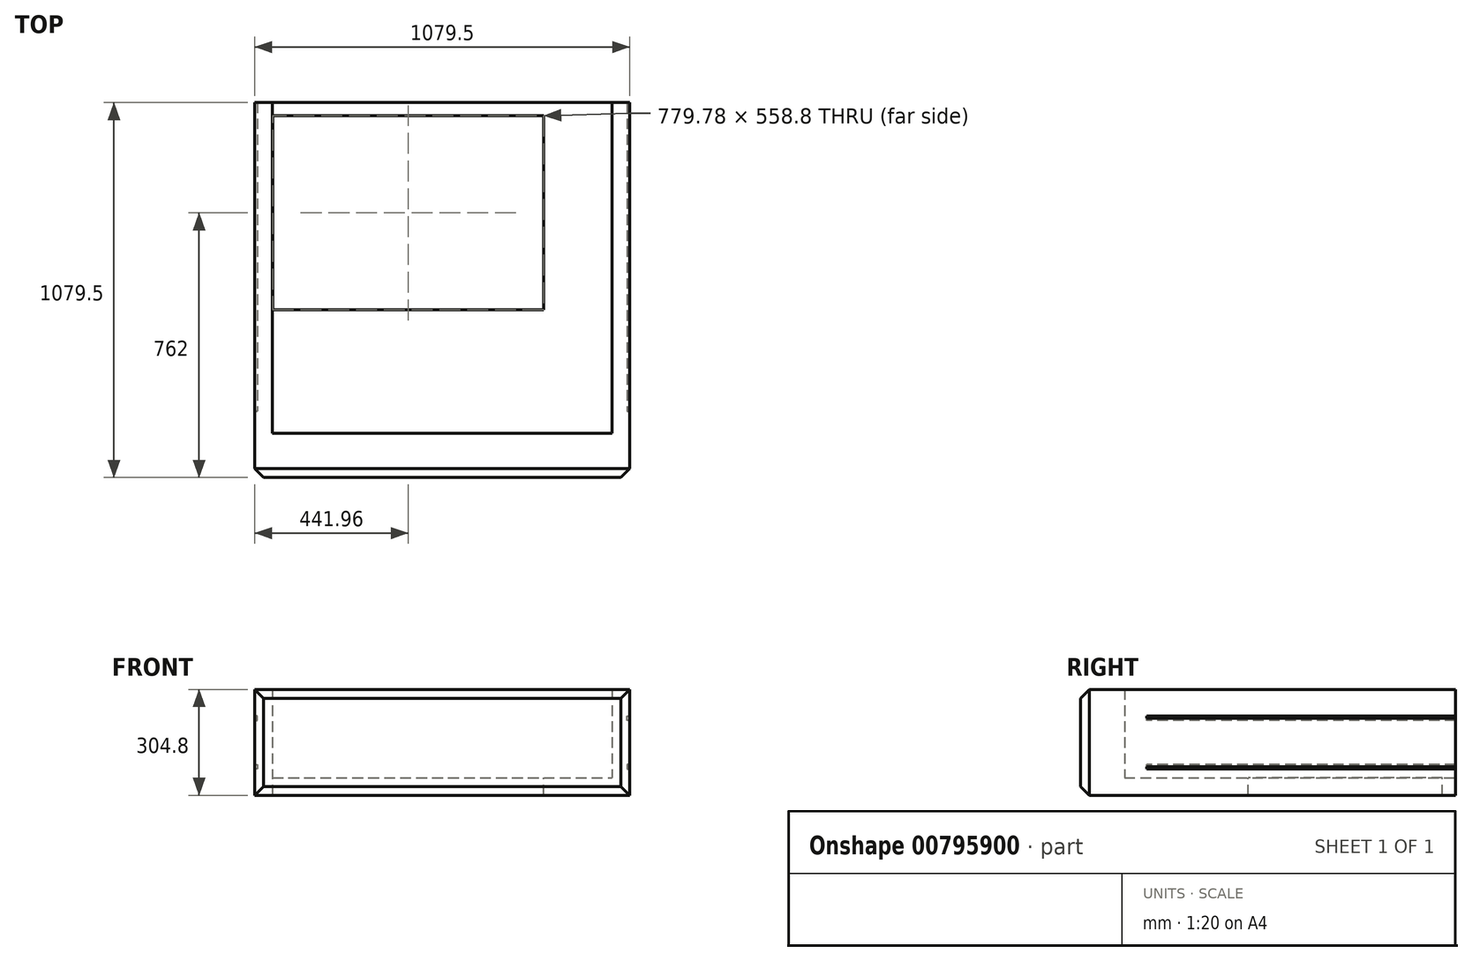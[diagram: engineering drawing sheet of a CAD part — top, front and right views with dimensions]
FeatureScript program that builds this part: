
annotation { "Feature Type Name" : "Feature", "Feature Type Description" : "" }
export const myFeature = defineFeature(function(context is Context, id is Id, definition is map)
    precondition{}
    {
        {
            var Q0;
            Q0=qCreatedBy(makeId("Top.planeOp"),FACE);
            var sketch = newSketch(context, id + "F0", { "sketchPlane" : qUnion([Q0])});
            skLineSegment(sketch, "E0.0", {"start": v(539.75, 254) * mm, "end": v(539.75, -825.5) * mm});
            skLineSegment(sketch, "E0.1", {"start": v(539.75, 254) * mm, "end": v(-539.75, 254) * mm});
            skLineSegment(sketch, "E0.2", {"start": v(-539.75, -825.5) * mm, "end": v(-539.75, 254) * mm});
            skLineSegment(sketch, "E0.3", {"start": v(-539.75, -825.5) * mm, "end": v(539.75, -825.5) * mm});
            skLineSegment(sketch, "E1.bottom", {"start": v(-474.98, 203.2) * mm, "end": v(279.4, 203.2) * mm});
            skLineSegment(sketch, "E1.top", {"start": v(-474.98, -330.2) * mm, "end": v(279.4, -330.2) * mm});
            skLineSegment(sketch, "E1.left", {"start": v(-474.98, 203.2) * mm, "end": v(-474.98, -330.2) * mm});
            skLineSegment(sketch, "E1.right", {"start": v(279.4, 203.2) * mm, "end": v(279.4, -330.2) * mm});
            skSolve(sketch);
        }
        {
            var Q0;
            Q0=makeQuery(id+"F0.imprint","IMPRINT",FACE,{"disambiguationData":[TD([[makeQuery(id+"F0.imprint","IMPRINT",EDGE,{"derivedFrom":sQuery(id+"F0.wireOp",EDGE,"E0.0")}),-1.0]])]});
            var sketch = newSketch(context, id + "F1", { "sketchPlane" : qUnion([Q0])});
            skLineSegment(sketch, "E2.0", {"start": v(539.75, 254) * mm, "end": v(488.95, 254) * mm});
            skLineSegment(sketch, "E2.1", {"start": v(539.75, 254) * mm, "end": v(539.75, -825.5) * mm});
            skLineSegment(sketch, "E2.2", {"start": v(-539.75, -825.5) * mm, "end": v(539.75, -825.5) * mm});
            skLineSegment(sketch, "E2.3", {"start": v(-539.75, -825.5) * mm, "end": v(-539.75, 254) * mm});
            skLineSegment(sketch, "E3.0", {"start": v(-488.95, -698.5) * mm, "end": v(488.95, -698.5) * mm});
            skLineSegment(sketch, "E3.1", {"start": v(-488.95, -698.5) * mm, "end": v(-488.95, 254) * mm});
            skLineSegment(sketch, "E3.3", {"start": v(488.95, 254) * mm, "end": v(488.95, -698.5) * mm});
            skLineSegment(sketch, "E4.trimOffspring", {"start": v(-488.95, 254) * mm, "end": v(-539.75, 254) * mm});
            skSolve(sketch);
        }
        {
            var Q0;
            Q0 = qSketchRegion(id + "F1", true);
            extrude(context, id + "F2", {"entities" : qUnion([Q0]), "depth" : 304.8 * mm, "offsetDistance" : 25.4 * mm});
        }
        {
            var Q0;
            Q0=qCreatedBy(makeId("Top.planeOp"),FACE);
            var sketch = newSketch(context, id + "F3", { "sketchPlane" : qUnion([Q0])});
            skLineSegment(sketch, "E5.bottom", {"start": v(-539.75, 254) * mm, "end": v(539.75, 254) * mm});
            skLineSegment(sketch, "E5.top", {"start": v(-539.75, -825.5) * mm, "end": v(539.75, -825.5) * mm});
            skLineSegment(sketch, "E5.left", {"start": v(-539.75, 254) * mm, "end": v(-539.75, -825.5) * mm});
            skLineSegment(sketch, "E5.right", {"start": v(539.75, 254) * mm, "end": v(539.75, -825.5) * mm});
            skSolve(sketch);
        }
        {
            var Q0;
            Q0 = qSketchRegion(id + "F3", true);
            extrude(context, id + "F4", {"entities" : qUnion([Q0]), "operationType" : NewBodyOperationType.ADD, "depth" : 50.8 * mm, "offsetDistance" : 25.4 * mm});
        }
        {
            var Q0;
            Q0=makeQuery(id+"F2.opExtrude","SWEPT_FACE",FACE,{"disambiguationData":[OSD([sQuery(id+"F1.wireOp",EDGE,"E2.2")])]});
            chamfer(context, id + "F5", {"entities" : qUnion([Q0]), "width" : 25.4 * mm, "tangentPropagation" : true});
        }
        {
            var Q0;
            Q0=makeQuery(id+"F2.opExtrude","SWEPT_FACE",FACE,{"disambiguationData":[OSD([sQuery(id+"F1.wireOp",EDGE,"E2.1")])]});
            var sketch = newSketch(context, id + "F6", { "sketchPlane" : qUnion([Q0])});
            skArc(sketch, "E6", {"start": v(39.93, 203.2) * mm, "mid": v(103.43, 139.7) * mm, "end": v(166.93, 203.2) * mm});
            skLineSegment(sketch, "E7", {"start": v(166.93, 203.2) * mm, "end": v(166.93, 304.8) * mm});
            skLineSegment(sketch, "E8", {"start": v(39.93, 203.2) * mm, "end": v(39.93, 304.8) * mm});
            skSolve(sketch);
        }
        {
            var Q0;
            Q0=makeQuery(id+"F4.opExtrude","CAP_FACE",FACE,{"disambiguationData":[OSD([sQuery(id+"F3.wireOp",EDGE,"E5.bottom"),sQuery(id+"F3.wireOp",EDGE,"E5.top"),sQuery(id+"F3.wireOp",EDGE,"E5.left"),sQuery(id+"F3.wireOp",EDGE,"E5.right")])],"isStart":false});
            var sketch = newSketch(context, id + "F7", { "sketchPlane" : qUnion([Q0])});
            skCircle(sketch, "E9", {"center": v(0, 0) * mm, "radius": 63.5 * mm});
            skSolve(sketch);
        }
        {
            var Q0;
            Q0=makeQuery(id+"F7.imprint","IMPRINT",FACE,{"disambiguationData":[TD([[makeQuery(id+"F7.imprint","IMPRINT",EDGE,{"derivedFrom":sQuery(id+"F7.wireOp",EDGE,"E9")}),1.0]])]});
            extrude(context, id + "F8", {"entities" : qUnion([Q0]), "operationType" : NewBodyOperationType.REMOVE, "endBound" : BoundingType.UP_TO_NEXT, "oppositeDirection" : true, "depth" : 25.4 * mm, "offsetDistance" : 25.4 * mm});
        }
        {
            var Q0;
            Q0=makeQuery(id+"F4.opExtrude","CAP_FACE",FACE,{"disambiguationData":[OSD([sQuery(id+"F3.wireOp",EDGE,"E5.bottom"),sQuery(id+"F3.wireOp",EDGE,"E5.top"),sQuery(id+"F3.wireOp",EDGE,"E5.left"),sQuery(id+"F3.wireOp",EDGE,"E5.right")])],"isStart":false});
            var sketch = newSketch(context, id + "F9", { "sketchPlane" : qUnion([Q0])});
            skLineSegment(sketch, "E10.0", {"start": v(-474.98, 203.2) * mm, "end": v(279.4, 203.2) * mm});
            skLineSegment(sketch, "E10.1", {"start": v(-474.98, 203.2) * mm, "end": v(-474.98, -330.2) * mm});
            skLineSegment(sketch, "E10.2", {"start": v(-474.98, -330.2) * mm, "end": v(279.4, -330.2) * mm});
            skLineSegment(sketch, "E10.3", {"start": v(279.4, 203.2) * mm, "end": v(279.4, -330.2) * mm});
            skLineSegment(sketch, "E11.0", {"start": v(-487.68, 215.9) * mm, "end": v(292.1, 215.9) * mm});
            skLineSegment(sketch, "E11.1", {"start": v(-487.68, 215.9) * mm, "end": v(-487.68, -342.9) * mm});
            skLineSegment(sketch, "E11.2", {"start": v(-487.68, -342.9) * mm, "end": v(292.1, -342.9) * mm});
            skLineSegment(sketch, "E11.3", {"start": v(292.1, 215.9) * mm, "end": v(292.1, -342.9) * mm});
            skSolve(sketch);
        }
        {
            var Q0;
            Q0=makeQuery(id+"F9.imprint","IMPRINT",FACE,{"disambiguationData":[TD([[makeQuery(id+"F9.imprint","IMPRINT",EDGE,{"derivedFrom":sQuery(id+"F9.wireOp",EDGE,"E10.0")}),1.0]])]});
            var Q1;
            Q1=makeQuery(id+"F9.imprint","IMPRINT",FACE,{"disambiguationData":[TD([[makeQuery(id+"F9.imprint","IMPRINT",EDGE,{"derivedFrom":sQuery(id+"F9.wireOp",EDGE,"E10.0")}),-1.0]])]});
            extrude(context, id + "F10", {"entities" : qUnion([Q0, Q1]), "operationType" : NewBodyOperationType.REMOVE, "endBound" : BoundingType.UP_TO_NEXT, "oppositeDirection" : true, "depth" : 25.4 * mm, "offsetDistance" : 25.4 * mm});
        }
        {
            var Q0;
            Q0=qCreatedBy(makeId("Front.planeOp"),FACE);
            var sketch = newSketch(context, id + "F11", { "sketchPlane" : qUnion([Q0])});
            skLineSegment(sketch, "E12", {"start": v(639.27, 152.4) * mm, "end": v(-587.53, 152.4) * mm, "construction": true});
            skPoint(sketch, "E12.startSnap0", {"position": v(557.43, 152.4) * mm});
            skLineSegment(sketch, "E13", {"start": v(557.43, 152.4) * mm, "end": v(557.43, 228.6) * mm});
            skLineSegment(sketch, "E14", {"start": v(557.43, 228.6) * mm, "end": v(532.03, 228.6) * mm});
            skLineSegment(sketch, "E15", {"start": v(532.03, 228.6) * mm, "end": v(532.03, 215.9) * mm});
            skLineSegment(sketch, "E16", {"start": v(532.03, 215.9) * mm, "end": v(538.38, 215.9) * mm});
            skLineSegment(sketch, "E17", {"start": v(538.38, 215.9) * mm, "end": v(538.38, 222.25) * mm});
            skLineSegment(sketch, "E18", {"start": v(538.38, 222.25) * mm, "end": v(551.08, 222.25) * mm});
            skLineSegment(sketch, "E19", {"start": v(551.08, 222.25) * mm, "end": v(551.08, 152.4) * mm});
            skLineSegment(sketch, "E20.MirrorCS", {"start": v(532.03, 88.9) * mm, "end": v(538.38, 88.9) * mm});
            skLineSegment(sketch, "E21.MirrorCS", {"start": v(538.38, 88.9) * mm, "end": v(538.38, 82.55) * mm});
            skLineSegment(sketch, "E22.MirrorCS", {"start": v(551.08, 82.55) * mm, "end": v(551.08, 152.4) * mm});
            skLineSegment(sketch, "E23.MirrorCS", {"start": v(538.38, 82.55) * mm, "end": v(551.08, 82.55) * mm});
            skLineSegment(sketch, "E24.MirrorCS", {"start": v(532.03, 76.2) * mm, "end": v(532.03, 88.9) * mm});
            skLineSegment(sketch, "E25.MirrorCS", {"start": v(557.43, 152.4) * mm, "end": v(557.43, 76.2) * mm});
            skLineSegment(sketch, "E26.MirrorCS", {"start": v(557.43, 76.2) * mm, "end": v(532.03, 76.2) * mm});
            skLineSegment(sketch, "E27", {"start": v(0, 119.97) * mm, "end": v(0, -99.2) * mm, "construction": true});
            skLineSegment(sketch, "E28.MirrorCS", {"start": v(-538.38, 88.9) * mm, "end": v(-538.38, 82.55) * mm});
            skLineSegment(sketch, "E29.MirrorCS", {"start": v(-532.03, 88.9) * mm, "end": v(-538.38, 88.9) * mm});
            skLineSegment(sketch, "E30.MirrorCS", {"start": v(-532.03, 76.2) * mm, "end": v(-532.03, 88.9) * mm});
            skLineSegment(sketch, "E31.MirrorCS", {"start": v(-538.38, 82.55) * mm, "end": v(-551.08, 82.55) * mm});
            skLineSegment(sketch, "E32.MirrorCS", {"start": v(-551.08, 82.55) * mm, "end": v(-551.08, 152.4) * mm});
            skLineSegment(sketch, "E33.MirrorCS", {"start": v(-557.43, 152.4) * mm, "end": v(-557.43, 76.2) * mm});
            skLineSegment(sketch, "E34.MirrorCS", {"start": v(-557.43, 76.2) * mm, "end": v(-532.03, 76.2) * mm});
            skLineSegment(sketch, "E35.MirrorCS", {"start": v(-538.38, 215.9) * mm, "end": v(-538.38, 222.25) * mm});
            skLineSegment(sketch, "E36.MirrorCS", {"start": v(-532.03, 215.9) * mm, "end": v(-538.38, 215.9) * mm});
            skLineSegment(sketch, "E37.MirrorCS", {"start": v(-557.43, 228.6) * mm, "end": v(-532.03, 228.6) * mm});
            skLineSegment(sketch, "E38.MirrorCS", {"start": v(-532.03, 228.6) * mm, "end": v(-532.03, 215.9) * mm});
            skLineSegment(sketch, "E39.MirrorCS", {"start": v(-538.38, 222.25) * mm, "end": v(-551.08, 222.25) * mm});
            skLineSegment(sketch, "E40.MirrorCS", {"start": v(-557.43, 152.4) * mm, "end": v(-557.43, 228.6) * mm});
            skLineSegment(sketch, "E41.MirrorCS", {"start": v(-551.08, 222.25) * mm, "end": v(-551.08, 152.4) * mm});
            skSolve(sketch);
        }
        {
            var Q0;
            Q0=makeQuery(id+"F11.imprint","IMPRINT",FACE,{"disambiguationData":[TD([[makeQuery(id+"F11.imprint","IMPRINT",EDGE,{"derivedFrom":sQuery(id+"F11.wireOp",EDGE,"E13")}),1.0]])]});
            var Q1;
            Q1=makeQuery(id+"F11.imprint","IMPRINT",FACE,{"disambiguationData":[TD([[makeQuery(id+"F11.imprint","IMPRINT",EDGE,{"derivedFrom":sQuery(id+"F11.wireOp",EDGE,"E28.MirrorCS")}),1.0]])]});
            var Q2;
            Q2=makeQuery(id+"F4.boolean.opBoolean","MERGE",FACE,{"derivedFrom":[makeQuery(id+"F2.opExtrude","SWEPT_FACE",FACE,{"disambiguationData":[OSD([sQuery(id+"F1.wireOp",EDGE,"E2.0")])]}),makeQuery(id+"F2.opExtrude","SWEPT_FACE",FACE,{"disambiguationData":[OSD([sQuery(id+"F1.wireOp",EDGE,"E4.trimOffspring")])]}),makeQuery(id+"F4.opExtrude","SWEPT_FACE",FACE,{"disambiguationData":[OSD([sQuery(id+"F3.wireOp",EDGE,"E5.bottom")])]})]});
            extrude(context, id + "F12", {"entities" : qUnion([Q0, Q1]), "operationType" : NewBodyOperationType.REMOVE, "endBound" : BoundingType.UP_TO_SURFACE, "oppositeDirection" : true, "depth" : 25.4 * mm, "endBoundEntityFace" : qUnion([Q2]), "offsetDistance" : 25.4 * mm, "hasSecondDirection" : true, "secondDirectionOppositeDirection" : false, "secondDirectionDepth" : 635 * mm});
        }
    });
